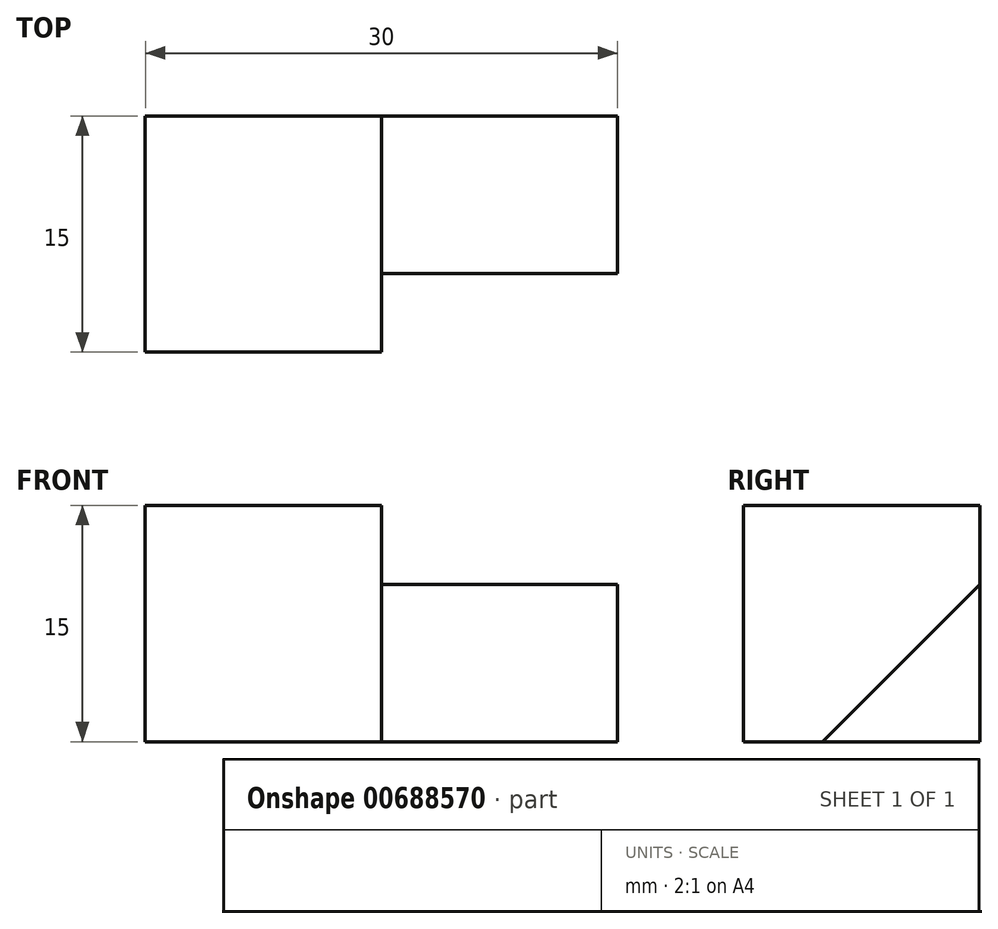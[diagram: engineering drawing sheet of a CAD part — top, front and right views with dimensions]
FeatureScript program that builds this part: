
annotation { "Feature Type Name" : "Feature", "Feature Type Description" : "" }
export const myFeature = defineFeature(function(context is Context, id is Id, definition is map)
    precondition{}
    {
        {
            var Q0;
            Q0=qCreatedBy(makeId("Top.planeOp"),FACE);
            var sketch = newSketch(context, id + "F0", { "sketchPlane" : qUnion([Q0])});
            skLineSegment(sketch, "E0.bottom", {"start": v(-3.66, -6.46) * mm, "end": v(11.34, -6.46) * mm});
            skLineSegment(sketch, "E0.top", {"start": v(-3.66, -21.46) * mm, "end": v(11.34, -21.46) * mm});
            skLineSegment(sketch, "E0.left", {"start": v(-3.66, -6.46) * mm, "end": v(-3.66, -21.46) * mm});
            skLineSegment(sketch, "E0.right", {"start": v(11.34, -6.46) * mm, "end": v(11.34, -21.46) * mm});
            skSolve(sketch);
        }
        {
            var Q0;
            Q0=qSketchRegion(id+"F0",true);
            extrude(context, id + "F1", {"entities" : qUnion([Q0]), "depth" : 15 * mm});
        }
        {
            var Q0;
            Q0=makeQuery(id+"F1.opExtrude","SWEPT_FACE",FACE,{"disambiguationData":[OSD([sQuery(id+"F0.wireOp",EDGE,"E0.right")])]});
            var sketch = newSketch(context, id + "F2", { "sketchPlane" : qUnion([Q0])});
            skLineSegment(sketch, "E1", {"start": v(-21.46, 0) * mm, "end": v(-16.46, 0) * mm});
            skLineSegment(sketch, "E2", {"start": v(-16.46, 0) * mm, "end": v(-6.46, 10) * mm});
            skLineSegment(sketch, "E3", {"start": v(-6.46, 10) * mm, "end": v(-6.46, 15) * mm});
            skSolve(sketch);
        }
        {
            var Q0;
            {var subQ0=sQuery(id+"F2.wireOp",EDGE,"E2");Q0=makeQuery(id+"F2.imprint","IMPRINT",FACE,{"disambiguationData":[TD([[makeQuery(id+"F2.imprint","IMPRINT",EDGE,{"derivedFrom":subQ0}),-1.0]])]});}
            extrude(context, id + "F3", {"entities" : qUnion([Q0]), "operationType" : NewBodyOperationType.ADD, "depth" : 15 * mm});
        }
    });
